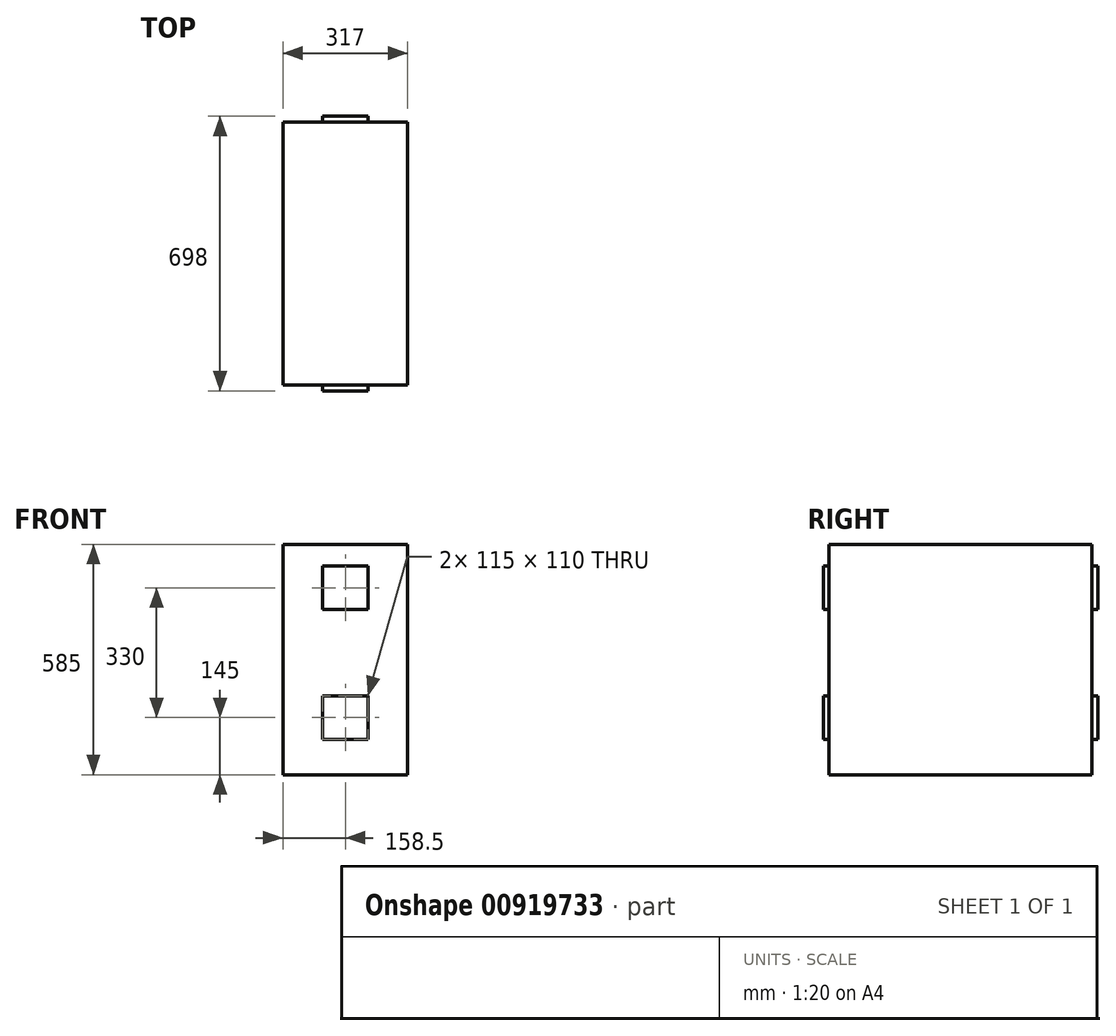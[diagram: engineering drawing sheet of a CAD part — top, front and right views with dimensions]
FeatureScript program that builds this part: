
annotation { "Feature Type Name" : "Feature", "Feature Type Description" : "" }
export const myFeature = defineFeature(function(context is Context, id is Id, definition is map)
    precondition{}
    {
        {
            var Q0;
            Q0=qCreatedBy(makeId("Front.planeOp"),FACE);
            var sketch = newSketch(context, id + "F0", { "sketchPlane" : qUnion([Q0])});
            skLineSegment(sketch, "E0.bottom", {"start": v(0, 0) * mm, "end": v(317, 0) * mm});
            skLineSegment(sketch, "E0.top", {"start": v(0, 585) * mm, "end": v(317, 585) * mm});
            skLineSegment(sketch, "E0.left", {"start": v(0, 0) * mm, "end": v(0, 585) * mm});
            skLineSegment(sketch, "E0.right", {"start": v(317, 0) * mm, "end": v(317, 585) * mm});
            skSolve(sketch);
        }
        {
            var Q0;
            Q0=makeQuery(id+"F0.imprint","IMPRINT",FACE,{"disambiguationData":[TD([[makeQuery(id+"F0.imprint","IMPRINT",EDGE,{"derivedFrom":sQuery(id+"F0.wireOp",EDGE,"E0.bottom")}),1.0]])]});
            extrude(context, id + "F1", {"entities" : qUnion([Q0]), "depth" : 668 * mm, "symmetric" : true});
        }
        {
            var Q0;
            Q0=makeQuery(id+"F1.opExtrude","CAP_FACE",FACE,{"disambiguationData":[OSD([sQuery(id+"F0.wireOp",EDGE,"E0.bottom"),sQuery(id+"F0.wireOp",EDGE,"E0.top"),sQuery(id+"F0.wireOp",EDGE,"E0.left"),sQuery(id+"F0.wireOp",EDGE,"E0.right")])],"isStart":false});
            var sketch = newSketch(context, id + "F2", { "sketchPlane" : qUnion([Q0])});
            skLineSegment(sketch, "E1.bottom", {"start": v(216, 90) * mm, "end": v(101, 90) * mm});
            skLineSegment(sketch, "E1.top", {"start": v(216, 200) * mm, "end": v(101, 200) * mm});
            skLineSegment(sketch, "E1.left", {"start": v(216, 90) * mm, "end": v(216, 200) * mm});
            skLineSegment(sketch, "E1.right", {"start": v(101, 90) * mm, "end": v(101, 200) * mm});
            skPoint(sketch, "E1.middle", {"position": v(158.5, 145) * mm});
            skPoint(sketch, "E1.middle.positionSnap0", {"position": v(158.5, 0) * mm});
            skPoint(sketch, "E1.centerSnap0", {"position": v(158.5, 0) * mm});
            skLineSegment(sketch, "E2.bottom", {"start": v(216, 420) * mm, "end": v(101, 420) * mm});
            skLineSegment(sketch, "E2.top", {"start": v(216, 530) * mm, "end": v(101, 530) * mm});
            skLineSegment(sketch, "E2.left", {"start": v(216, 420) * mm, "end": v(216, 530) * mm});
            skLineSegment(sketch, "E2.right", {"start": v(101, 420) * mm, "end": v(101, 530) * mm});
            skPoint(sketch, "E2.middle", {"position": v(158.5, 475) * mm});
            skSolve(sketch);
        }
        {
            var Q0;
            Q0=makeQuery(id+"F2.imprint","IMPRINT",FACE,{"disambiguationData":[TD([[makeQuery(id+"F2.imprint","IMPRINT",EDGE,{"derivedFrom":sQuery(id+"F2.wireOp",EDGE,"E2.bottom")}),-1.0]])]});
            var Q1;
            Q1=makeQuery(id+"F2.imprint","IMPRINT",FACE,{"disambiguationData":[TD([[makeQuery(id+"F2.imprint","IMPRINT",EDGE,{"derivedFrom":sQuery(id+"F2.wireOp",EDGE,"E1.bottom")}),-1.0]])]});
            extrude(context, id + "F3", {"entities" : qUnion([Q0, Q1]), "operationType" : NewBodyOperationType.ADD, "depth" : 15 * mm, "offsetDistance" : 25 * mm});
        }
        {
            var Q0;
            Q0=makeQuery(id+"F1.opExtrude","CAP_FACE",FACE,{"disambiguationData":[OSD([sQuery(id+"F0.wireOp",EDGE,"E0.bottom"),sQuery(id+"F0.wireOp",EDGE,"E0.top"),sQuery(id+"F0.wireOp",EDGE,"E0.left"),sQuery(id+"F0.wireOp",EDGE,"E0.right")])],"isStart":true});
            var sketch = newSketch(context, id + "F4", { "sketchPlane" : qUnion([Q0])});
            skLineSegment(sketch, "E3.0.0", {"start": v(0, 585) * mm, "end": v(-317, 585) * mm});
            skLineSegment(sketch, "E3.0.1", {"start": v(-317, 585) * mm, "end": v(-317, 0) * mm});
            skLineSegment(sketch, "E3.0.2", {"start": v(-317, 0) * mm, "end": v(0, 0) * mm});
            skLineSegment(sketch, "E3.0.3", {"start": v(0, 0) * mm, "end": v(0, 585) * mm});
            skLineSegment(sketch, "E4.bottom", {"start": v(-101, 90) * mm, "end": v(-216, 90) * mm});
            skLineSegment(sketch, "E4.top", {"start": v(-101, 200) * mm, "end": v(-216, 200) * mm});
            skLineSegment(sketch, "E4.left", {"start": v(-101, 90) * mm, "end": v(-101, 200) * mm});
            skLineSegment(sketch, "E4.right", {"start": v(-216, 90) * mm, "end": v(-216, 200) * mm});
            skPoint(sketch, "E4.middle", {"position": v(-158.5, 145) * mm});
            skLineSegment(sketch, "E5.bottom", {"start": v(-101, 420) * mm, "end": v(-216, 420) * mm});
            skLineSegment(sketch, "E5.top", {"start": v(-101, 530) * mm, "end": v(-216, 530) * mm});
            skLineSegment(sketch, "E5.left", {"start": v(-101, 420) * mm, "end": v(-101, 530) * mm});
            skLineSegment(sketch, "E5.right", {"start": v(-216, 420) * mm, "end": v(-216, 530) * mm});
            skPoint(sketch, "E5.middle", {"position": v(-158.5, 475) * mm});
            skLineSegment(sketch, "E6", {"start": v(-158.5, 585) * mm, "end": v(-158.5, 0) * mm, "construction": true});
            skSolve(sketch);
        }
        {
            var Q0;
            Q0=makeQuery(id+"F4.imprint","IMPRINT",FACE,{"disambiguationData":[TD([[makeQuery(id+"F4.imprint","IMPRINT",EDGE,{"derivedFrom":sQuery(id+"F4.wireOp",EDGE,"E5.bottom")}),-1.0]])]});
            var Q1;
            Q1=makeQuery(id+"F4.imprint","IMPRINT",FACE,{"disambiguationData":[TD([[makeQuery(id+"F4.imprint","IMPRINT",EDGE,{"derivedFrom":sQuery(id+"F4.wireOp",EDGE,"E4.bottom")}),-1.0]])]});
            extrude(context, id + "F5", {"entities" : qUnion([Q0, Q1]), "operationType" : NewBodyOperationType.ADD, "depth" : 15 * mm, "offsetDistance" : 25 * mm});
        }
    });
